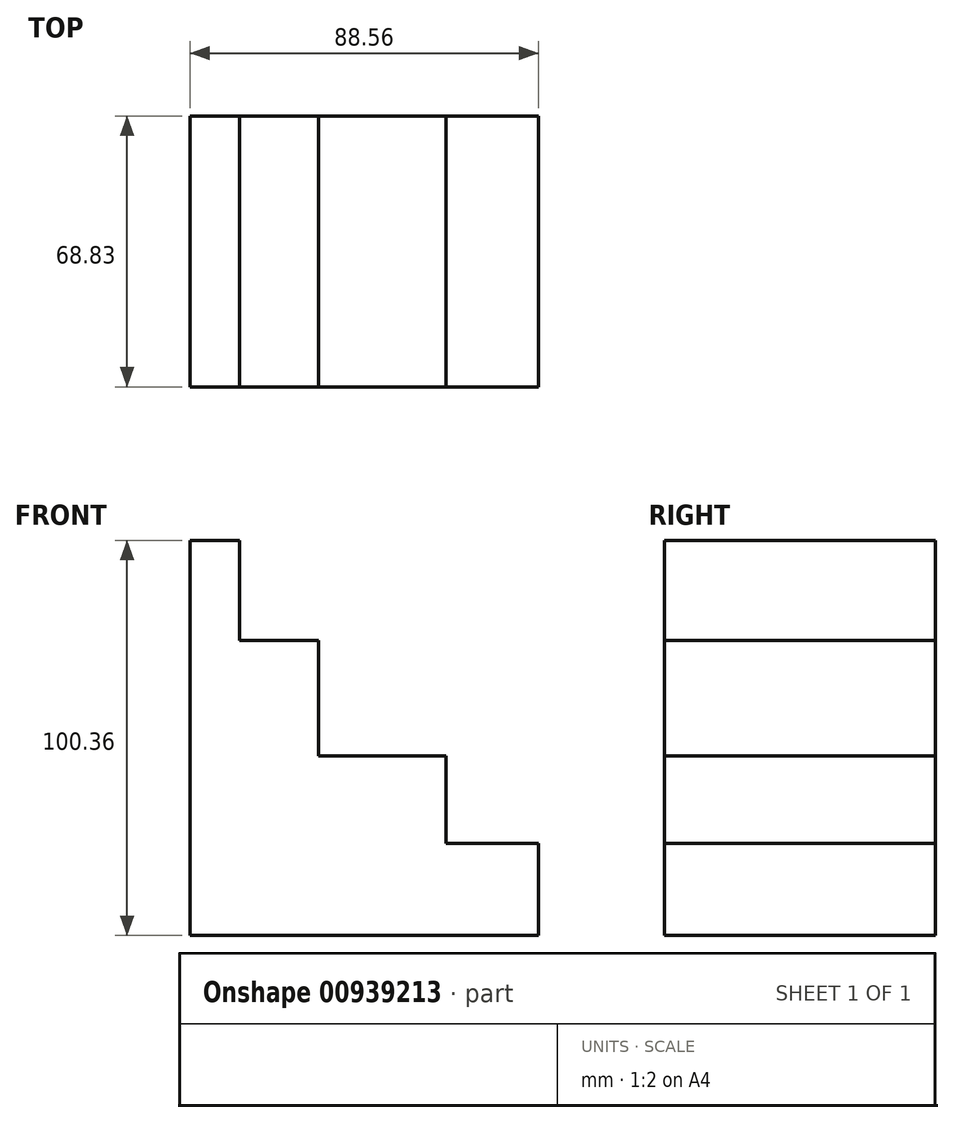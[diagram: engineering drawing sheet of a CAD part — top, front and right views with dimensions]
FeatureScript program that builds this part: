
annotation { "Feature Type Name" : "Feature", "Feature Type Description" : "" }
export const myFeature = defineFeature(function(context is Context, id is Id, definition is map)
    precondition{}
    {
        {
            var Q0;
            Q0=qCreatedBy(makeId("Front.planeOp"),FACE);
            var sketch = newSketch(context, id + "F0", { "sketchPlane" : qUnion([Q0])});
            skLineSegment(sketch, "E0", {"start": v(-44.03, 48.05) * mm, "end": v(-44.03, -52.31) * mm});
            skLineSegment(sketch, "E1", {"start": v(-44.03, -52.31) * mm, "end": v(44.53, -52.31) * mm});
            skLineSegment(sketch, "E2", {"start": v(44.53, -52.31) * mm, "end": v(44.53, -28.98) * mm});
            skLineSegment(sketch, "E3", {"start": v(44.53, -28.98) * mm, "end": v(20.95, -28.98) * mm});
            skLineSegment(sketch, "E4", {"start": v(20.95, -28.98) * mm, "end": v(20.95, -6.65) * mm});
            skLineSegment(sketch, "E5", {"start": v(20.95, -6.65) * mm, "end": v(-11.42, -6.65) * mm});
            skLineSegment(sketch, "E6", {"start": v(-11.42, -6.65) * mm, "end": v(-11.42, 22.7) * mm});
            skLineSegment(sketch, "E7", {"start": v(-11.42, 22.7) * mm, "end": v(-31.49, 22.7) * mm});
            skLineSegment(sketch, "E8", {"start": v(-31.49, 22.7) * mm, "end": v(-31.49, 48.05) * mm});
            skLineSegment(sketch, "E9", {"start": v(-31.49, 48.05) * mm, "end": v(-44.03, 48.05) * mm});
            skSolve(sketch);
        }
        {
            var Q0;
            Q0 = qSketchRegion(id + "F0", true);
            extrude(context, id + "F1", {"entities" : qUnion([Q0]), "depth" : 68.83 * mm, "offsetDistance" : 25.4 * mm});
        }
    });
